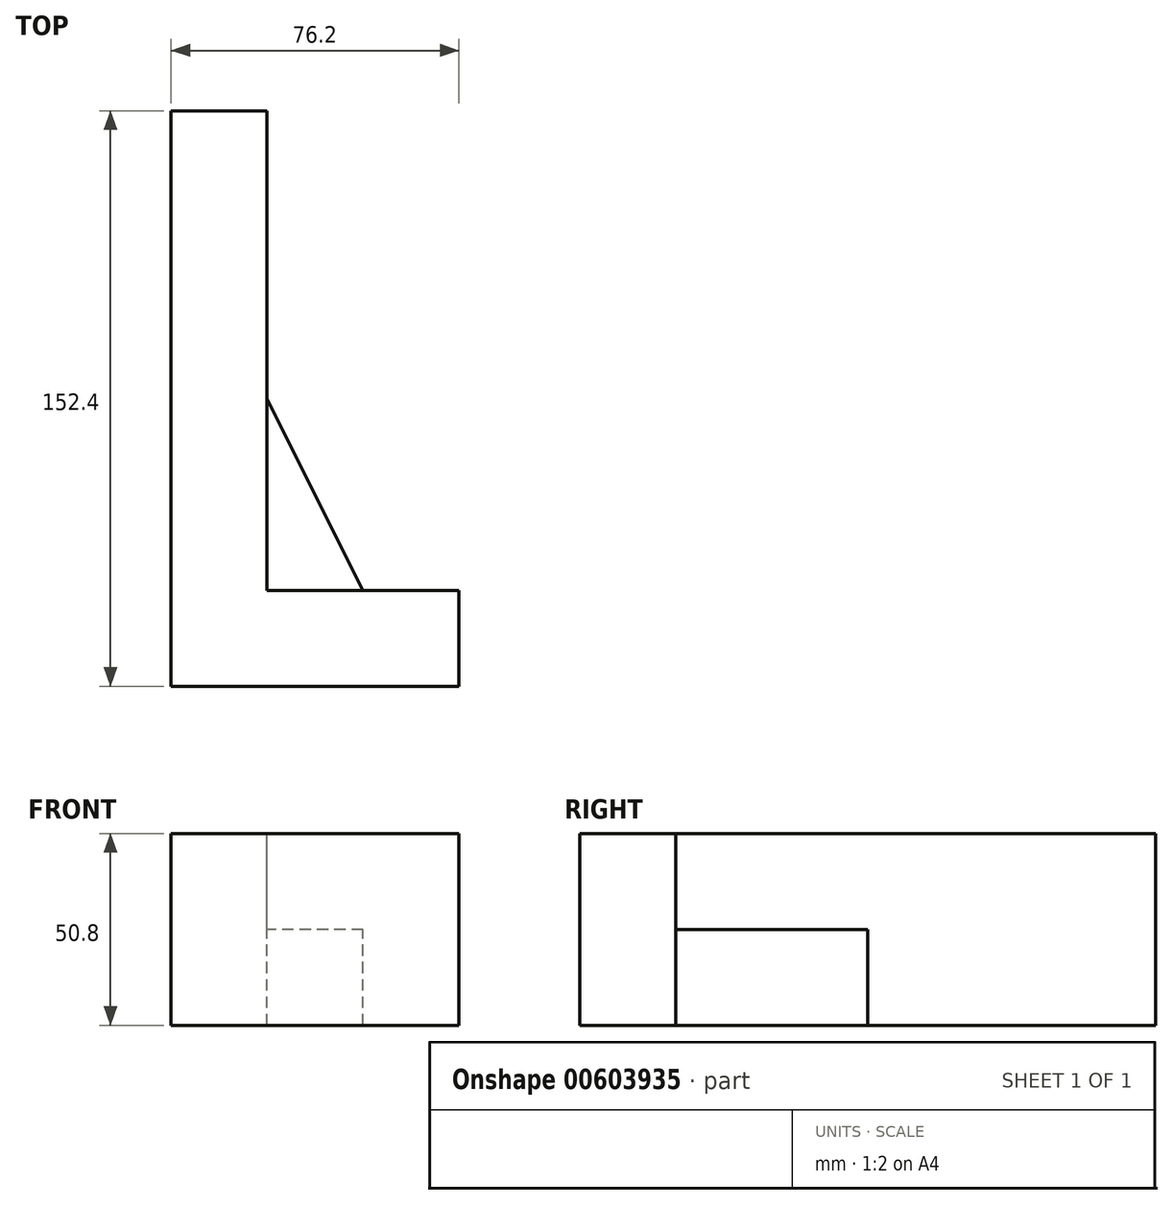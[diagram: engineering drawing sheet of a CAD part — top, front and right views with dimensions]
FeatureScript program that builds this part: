
annotation { "Feature Type Name" : "Feature", "Feature Type Description" : "" }
export const myFeature = defineFeature(function(context is Context, id is Id, definition is map)
    precondition{}
    {
        {
            var Q0;
            Q0=qCreatedBy(makeId("Front.planeOp"),FACE);
            var sketch = newSketch(context, id + "F0", { "sketchPlane" : qUnion([Q0])});
            skLineSegment(sketch, "E0.bottom", {"start": v(0, 0) * mm, "end": v(76.2, 0) * mm});
            skLineSegment(sketch, "E0.top", {"start": v(0, 50.8) * mm, "end": v(76.2, 50.8) * mm});
            skLineSegment(sketch, "E0.left", {"start": v(0, 0) * mm, "end": v(0, 50.8) * mm});
            skLineSegment(sketch, "E0.right", {"start": v(76.2, 0) * mm, "end": v(76.2, 50.8) * mm});
            skSolve(sketch);
        }
        {
            var Q0;
            Q0=makeQuery(id+"F0.imprint","IMPRINT",FACE,{"disambiguationData":[TD([[makeQuery(id+"F0.imprint","IMPRINT",EDGE,{"derivedFrom":sQuery(id+"F0.wireOp",EDGE,"E0.bottom")}),1.0]])]});
            extrude(context, id + "F1", {"entities" : qUnion([Q0]), "oppositeDirection" : true, "depth" : 152.4 * mm, "offsetDistance" : 25.4 * mm});
        }
        {
            var Q0;
            Q0=makeQuery(id+"F1.opExtrude","SWEPT_FACE",FACE,{"disambiguationData":[OSD([sQuery(id+"F0.wireOp",EDGE,"E0.top")])]});
            var sketch = newSketch(context, id + "F2", { "sketchPlane" : qUnion([Q0])});
            skLineSegment(sketch, "E1.bottom", {"start": v(76.2, 152.4) * mm, "end": v(25.4, 152.4) * mm});
            skLineSegment(sketch, "E1.top", {"start": v(76.2, 25.4) * mm, "end": v(25.4, 25.4) * mm});
            skLineSegment(sketch, "E1.left", {"start": v(76.2, 152.4) * mm, "end": v(76.2, 25.4) * mm});
            skLineSegment(sketch, "E1.right", {"start": v(25.4, 152.4) * mm, "end": v(25.4, 25.4) * mm});
            skSolve(sketch);
        }
        {
            var Q0;
            Q0=makeQuery(id+"F2.imprint","IMPRINT",FACE,{"disambiguationData":[TD([[makeQuery(id+"F2.imprint","IMPRINT",EDGE,{"derivedFrom":sQuery(id+"F2.wireOp",EDGE,"E1.bottom")}),-1.0]])]});
            extrude(context, id + "F3", {"entities" : qUnion([Q0]), "operationType" : NewBodyOperationType.REMOVE, "oppositeDirection" : true, "depth" : 50.8 * mm, "offsetDistance" : 25.4 * mm});
        }
        {
            var Q0;
            Q0=makeQuery(id+"F3.boolean.opBoolean","COPY",FACE,{"derivedFrom":makeQuery(id+"F3.opExtrude","SWEPT_FACE",FACE,{"disambiguationData":[OSD([sQuery(id+"F2.wireOp",EDGE,"E1.right")])]})});
            var sketch = newSketch(context, id + "F4", { "sketchPlane" : qUnion([Q0])});
            skLineSegment(sketch, "E2.bottom", {"start": v(25.4, 0) * mm, "end": v(76.2, 0) * mm});
            skLineSegment(sketch, "E2.top", {"start": v(25.4, 25.4) * mm, "end": v(76.2, 25.4) * mm});
            skLineSegment(sketch, "E2.left", {"start": v(25.4, 0) * mm, "end": v(25.4, 25.4) * mm});
            skLineSegment(sketch, "E2.right", {"start": v(76.2, 0) * mm, "end": v(76.2, 25.4) * mm});
            skSolve(sketch);
        }
        {
            var Q0;
            Q0=makeQuery(id+"F4.imprint","IMPRINT",FACE,{"disambiguationData":[TD([[makeQuery(id+"F4.imprint","IMPRINT",EDGE,{"derivedFrom":sQuery(id+"F4.wireOp",EDGE,"E2.bottom")}),-1.0]])]});
            extrude(context, id + "F5", {"entities" : qUnion([Q0]), "operationType" : NewBodyOperationType.ADD, "depth" : 25.4 * mm, "offsetDistance" : 25.4 * mm});
        }
        {
            var Q0;
            Q0=makeQuery(id+"F5.opExtrude","SWEPT_FACE",FACE,{"disambiguationData":[OSD([sQuery(id+"F4.wireOp",EDGE,"E2.top")])]});
            var sketch = newSketch(context, id + "F6", { "sketchPlane" : qUnion([Q0])});
            skLineSegment(sketch, "E3", {"start": v(25.4, 76.2) * mm, "end": v(50.8, 25.4) * mm});
            skSolve(sketch);
        }
        {
            var Q0;
            Q0=makeQuery(id+"F6.imprint","IMPRINT",FACE,{"disambiguationData":[TD([[makeQuery(id+"F6.imprint","IMPRINT",EDGE,{"derivedFrom":sQuery(id+"F6.wireOp",EDGE,"E3")}),1.0]])]});
            extrude(context, id + "F7", {"entities" : qUnion([Q0]), "operationType" : NewBodyOperationType.REMOVE, "oppositeDirection" : true, "depth" : 25.4 * mm, "offsetDistance" : 25.4 * mm});
        }
    });
